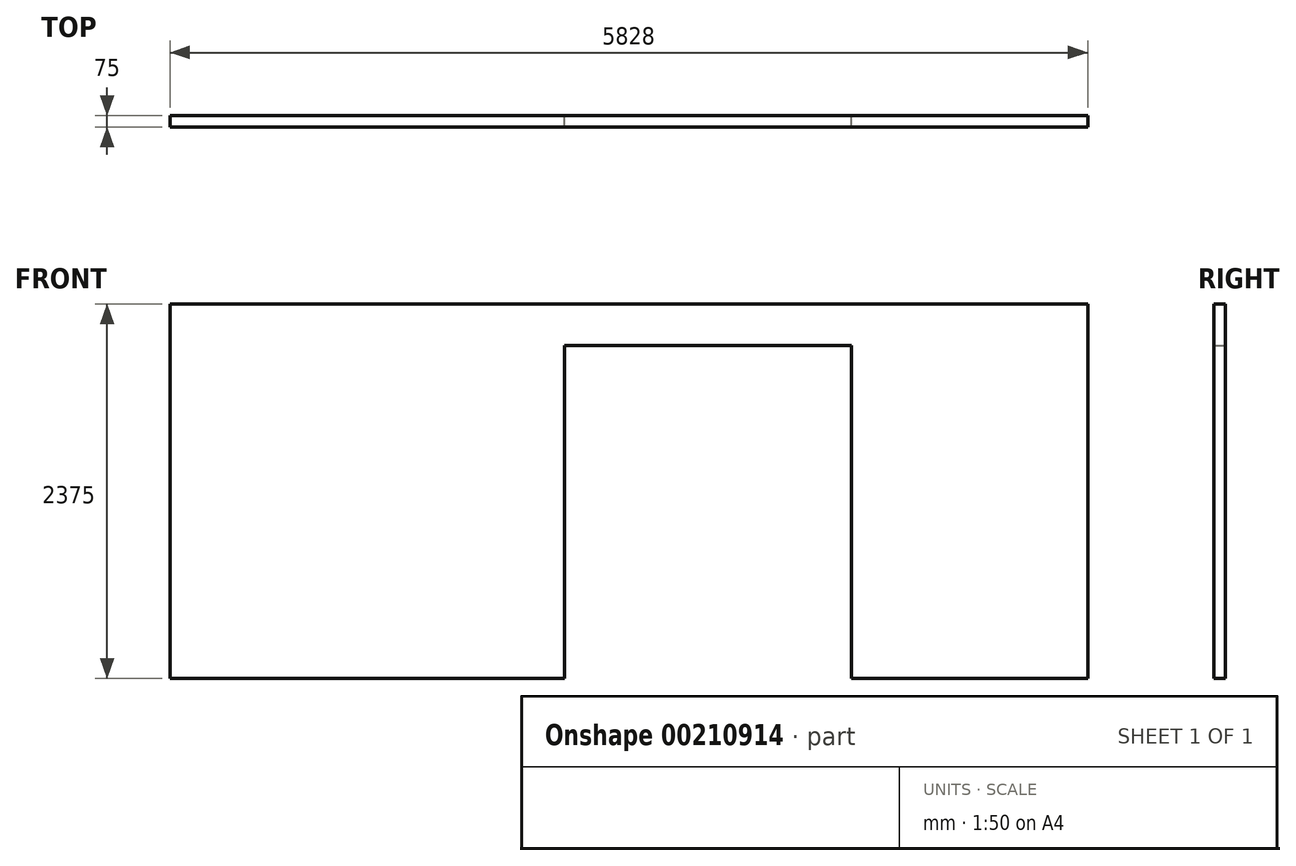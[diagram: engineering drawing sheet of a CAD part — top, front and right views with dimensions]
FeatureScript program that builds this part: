
annotation { "Feature Type Name" : "Feature", "Feature Type Description" : "" }
export const myFeature = defineFeature(function(context is Context, id is Id, definition is map)
    precondition{}
    {
        {
            var Q0;
            Q0=qCreatedBy(makeId("Front.planeOp"),FACE);
            var sketch = newSketch(context, id + "F0", { "sketchPlane" : qUnion([Q0])});
            skLineSegment(sketch, "E0.bottom", {"start": v(0, 0) * mm, "end": v(5828, 0) * mm});
            skLineSegment(sketch, "E0.right", {"start": v(5828, 0) * mm, "end": v(5828, 2375) * mm});
            skLineSegment(sketch, "E1", {"start": v(0, 2375) * mm, "end": v(5828, 2375) * mm});
            skLineSegment(sketch, "E2", {"start": v(0, 0) * mm, "end": v(0, 2375) * mm});
            skLineSegment(sketch, "E3.bottom", {"start": v(2506, 0) * mm, "end": v(4328, 0) * mm});
            skLineSegment(sketch, "E3.top", {"start": v(2506, 2112) * mm, "end": v(4328, 2112) * mm});
            skLineSegment(sketch, "E3.left", {"start": v(2506, 0) * mm, "end": v(2506, 2112) * mm});
            skLineSegment(sketch, "E3.right", {"start": v(4328, 0) * mm, "end": v(4328, 2112) * mm});
            skSolve(sketch);
        }
        {
            var Q0;
            Q0=makeQuery(id+"F0.imprint","IMPRINT",FACE,{"disambiguationData":[TD([[makeQuery(id+"F0.imprint","IMPRINT",EDGE,{"derivedFrom":sQuery(id+"F0.wireOp",EDGE,"E0.bottom")}),1.0]])]});
            extrude(context, id + "F1", {"entities" : qUnion([Q0]), "depth" : 75 * mm});
        }
    });
